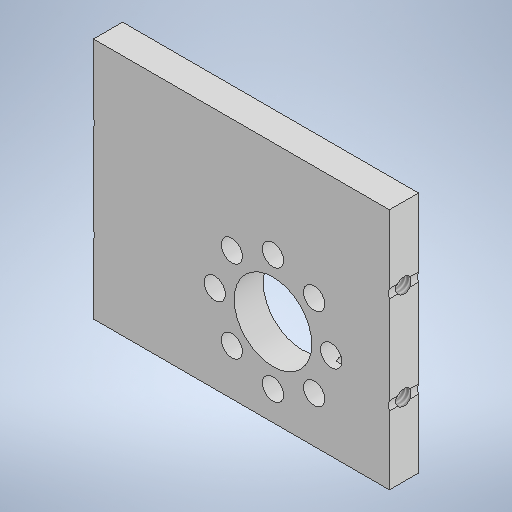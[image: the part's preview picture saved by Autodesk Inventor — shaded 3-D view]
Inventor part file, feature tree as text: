
AUTODESK INVENTOR PART (.ipt)
format: ipt  version: 2025.1 (Build 291241000, 241)  size: 320,512 bytes
history: native  units: mm
features: sketch x5, extrude x3, other x2, hole x2
ambient origin geometry x8: Origin, YZ Plane, XZ Plane, XY Plane, X Axis, Y Axis, Z Axis, Center Point
bodies: Body1 (feature_tree)
feature tree (12):
  other  "ソリッド1"
  extrude  "押し出し1"  Depth=30.5mm
  extrude  "押し出し2"  Depth=25.0mm
  hole  "穴2"  [1 undecoded]
  hole  "穴3"  [1 undecoded]
  extrude  "押し出し3"  Depth=2.2mm
  sketch  "スケッチ1"
  sketch  "スケッチ3"
  other  "スケッチ円形状パターン1"
  sketch  "スケッチ4"
  sketch  "スケッチ5"
  sketch  "スケッチ6"
note: 2 required parameter values undecoded (feature->parameter linkage not recoverable at this tier; creation-order binding heuristic only, values carry confidence <= 0.55)
